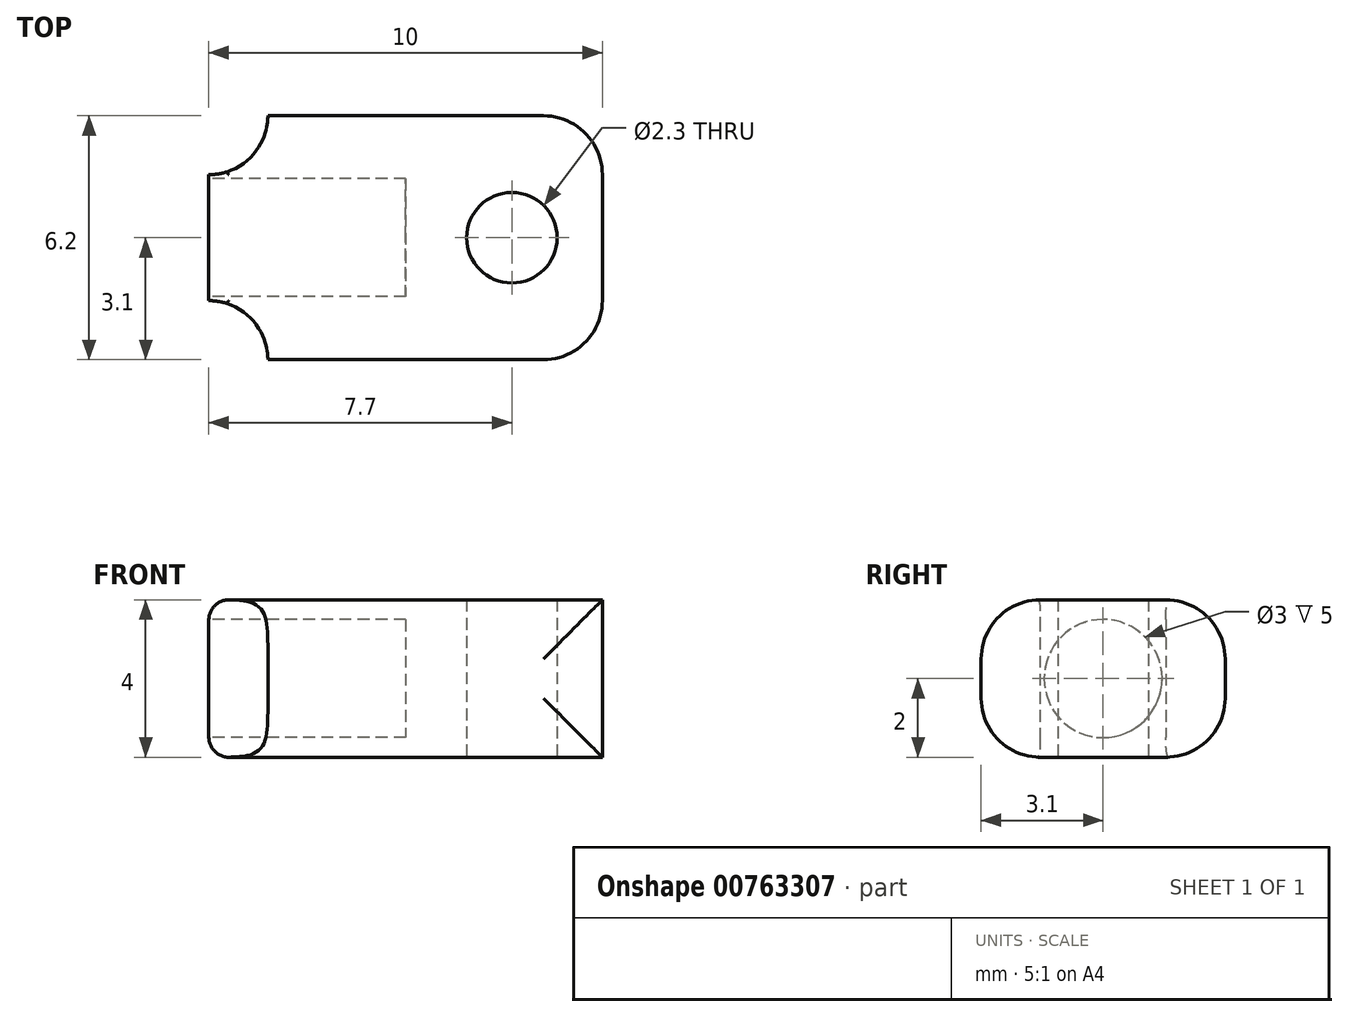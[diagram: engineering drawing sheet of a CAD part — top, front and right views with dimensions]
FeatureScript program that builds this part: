
annotation { "Feature Type Name" : "Feature", "Feature Type Description" : "" }
export const myFeature = defineFeature(function(context is Context, id is Id, definition is map)
    precondition{}
    {
        {
            var Q0;
            Q0=qCreatedBy(makeId("Top.planeOp"),FACE);
            var sketch = newSketch(context, id + "F0", { "sketchPlane" : qUnion([Q0])});
            skLineSegment(sketch, "E0.bottom", {"start": v(-3.5, 3.1) * mm, "end": v(5, 3.1) * mm});
            skLineSegment(sketch, "E0.top", {"start": v(-3.5, -3.1) * mm, "end": v(5, -3.1) * mm});
            skLineSegment(sketch, "E0.left", {"start": v(-5, 1.6) * mm, "end": v(-5, -1.6) * mm});
            skLineSegment(sketch, "E0.right", {"start": v(5, 3.1) * mm, "end": v(5, -3.1) * mm});
            skPoint(sketch, "E0.middle", {"position": v(0, 0) * mm});
            skArc(sketch, "E1", {"start": v(-5, 1.6) * mm, "mid": v(-3.94, 2.04) * mm, "end": v(-3.5, 3.1) * mm});
            skArc(sketch, "E2.MirrorCS", {"start": v(-5, -1.6) * mm, "mid": v(-3.94, -2.04) * mm, "end": v(-3.5, -3.1) * mm});
            skCircle(sketch, "E3", {"center": v(2.7, 0) * mm, "radius": 1.15 * mm});
            skSolve(sketch);
        }
        {
            var Q0;
            Q0 = qSketchRegion(id + "F0", true);
            extrude(context, id + "F1", {"entities" : qUnion([Q0]), "depth" : 4 * mm, "offsetDistance" : 25 * mm});
        }
        {
            var Q0;
            Q0=makeQuery(id+"F1.opExtrude","SWEPT_FACE",FACE,{"disambiguationData":[OSD([sQuery(id+"F0.wireOp",EDGE,"E0.left")])]});
            var sketch = newSketch(context, id + "F2", { "sketchPlane" : qUnion([Q0])});
            skCircle(sketch, "E4", {"center": v(0, 2) * mm, "radius": 1.5 * mm});
            skPoint(sketch, "E4.centerSnap0", {"position": v(-1.6, 2) * mm});
            skPoint(sketch, "E4.centerSnap1", {"position": v(0, 0) * mm});
            skSolve(sketch);
        }
        {
            var Q0;
            Q0 = qSketchRegion(id + "F2", true);
            extrude(context, id + "F3", {"entities" : qUnion([Q0]), "operationType" : NewBodyOperationType.REMOVE, "oppositeDirection" : true, "depth" : 5 * mm, "offsetDistance" : 25 * mm});
        }
        {
            var Q0;
            Q0=makeQuery(id+"F1.opExtrude","CAP_EDGE",EDGE,{"disambiguationData":[OSD([sQuery(id+"F0.wireOp",EDGE,"E0.bottom")])],"isStart":false});
            var Q1;
            Q1=makeQuery(id+"F1.opExtrude","CAP_EDGE",EDGE,{"disambiguationData":[OSD([sQuery(id+"F0.wireOp",EDGE,"E0.bottom")])],"isStart":true});
            var Q2;
            Q2=makeQuery(id+"F1.opExtrude","SWEPT_EDGE",EDGE,{"disambiguationData":[OSD([sQuery(id+"F0.wireOp",EDGE,"E0.bottom"),sQuery(id+"F0.wireOp",EDGE,"E0.right")])]});
            var Q3;
            Q3=makeQuery(id+"F1.opExtrude","SWEPT_EDGE",EDGE,{"disambiguationData":[OSD([sQuery(id+"F0.wireOp",EDGE,"E0.top"),sQuery(id+"F0.wireOp",EDGE,"E0.right")])]});
            var Q4;
            Q4=makeQuery(id+"F1.opExtrude","CAP_EDGE",EDGE,{"disambiguationData":[OSD([sQuery(id+"F0.wireOp",EDGE,"E0.top")])],"isStart":true});
            var Q5;
            Q5=makeQuery(id+"F1.opExtrude","CAP_EDGE",EDGE,{"disambiguationData":[OSD([sQuery(id+"F0.wireOp",EDGE,"E0.top")])],"isStart":false});
            fillet(context, id + "F4", {"entities" : qUnion([Q0, Q1, Q2, Q3, Q4, Q5]), "radius" : 1.5 * mm, "tangentPropagation" : true, "allowEdgeOverflow" : false});
        }
        {
            var Q0;
            Q0=makeQuery(id+"F1.opExtrude","CAP_EDGE",EDGE,{"disambiguationData":[OSD([sQuery(id+"F0.wireOp",EDGE,"E0.left")])],"isStart":false});
            var Q1;
            Q1=makeQuery(id+"F1.opExtrude","CAP_EDGE",EDGE,{"disambiguationData":[OSD([sQuery(id+"F0.wireOp",EDGE,"E0.left")])],"isStart":true});
            fillet(context, id + "F5", {"entities" : qUnion([Q0, Q1]), "radius" : .5 * mm, "tangentPropagation" : true, "allowEdgeOverflow" : false});
        }
    });
